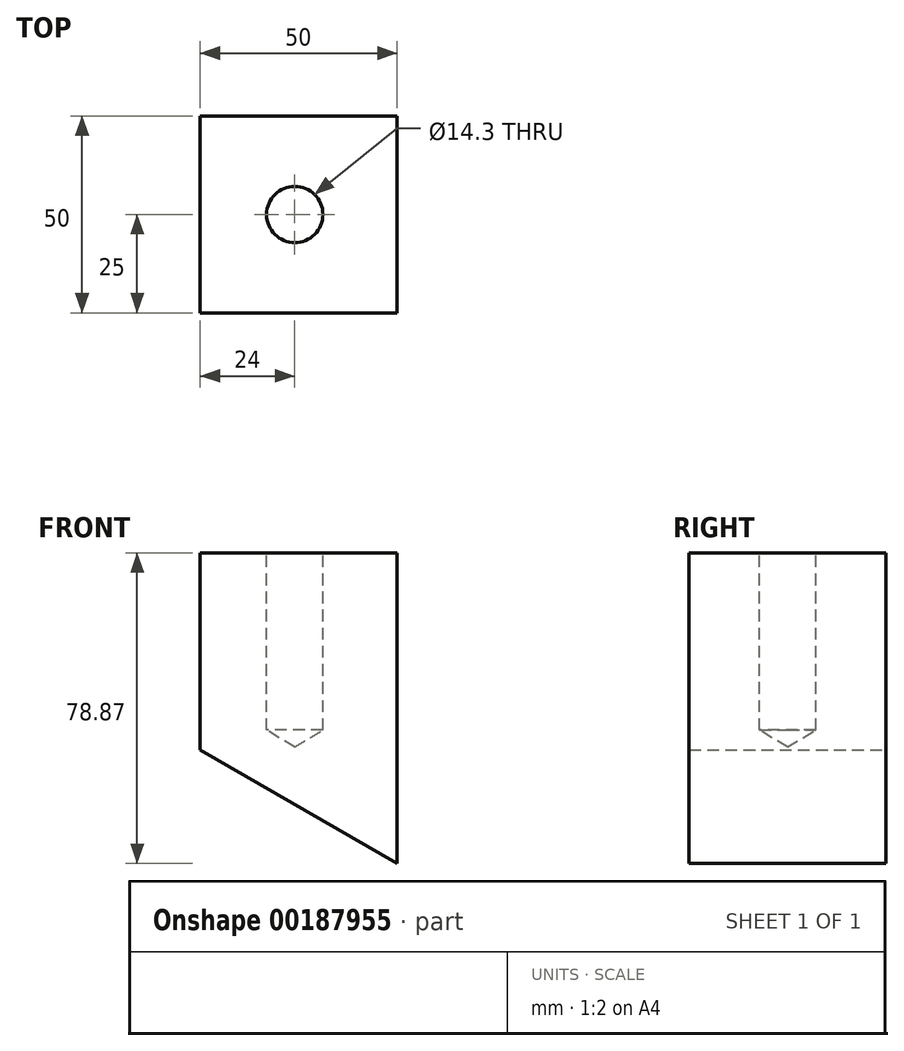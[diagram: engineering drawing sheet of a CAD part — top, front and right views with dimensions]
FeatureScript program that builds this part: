
annotation { "Feature Type Name" : "Feature", "Feature Type Description" : "" }
export const myFeature = defineFeature(function(context is Context, id is Id, definition is map)
    precondition{}
    {
        {
            var Q0;
            Q0=qCreatedBy(makeId("Front.planeOp"),FACE);
            var sketch = newSketch(context, id + "F0", { "sketchPlane" : qUnion([Q0])});
            skLineSegment(sketch, "E0", {"start": v(0, 0) * mm, "end": v(-24, 0) * mm});
            skLineSegment(sketch, "E1", {"start": v(-24, 0) * mm, "end": v(-24, -50) * mm});
            skLineSegment(sketch, "E2", {"start": v(-24, -50) * mm, "end": v(26, -78.87) * mm});
            skLineSegment(sketch, "E3", {"start": v(26, -78.87) * mm, "end": v(26, 0) * mm});
            skLineSegment(sketch, "E4", {"start": v(26, 0) * mm, "end": v(0, 0) * mm});
            skSolve(sketch);
        }
        {
            var Q0;
            Q0=makeQuery(id+"F0.imprint","IMPRINT",FACE,{"disambiguationData":[TD([[makeQuery(id+"F0.imprint","IMPRINT",EDGE,{"derivedFrom":sQuery(id+"F0.wireOp",EDGE,"E0")}),1.0]])]});
            extrude(context, id + "F1", {"entities" : qUnion([Q0]), "endBound" : BoundingType.SYMMETRIC, "depth" : 50 * mm});
        }
        {
            var Q0;
            Q0=makeQuery(id+"F1.opExtrude","SWEPT_FACE",FACE,{"disambiguationData":[OSD([sQuery(id+"F0.wireOp",EDGE,"E0"),sQuery(id+"F0.wireOp",EDGE,"E4")])]});
            var sketch = newSketch(context, id + "F2", { "sketchPlane" : qUnion([Q0])});
            skPoint(sketch, "E5", {"position": v(0, 0) * mm});
            skSolve(sketch);
        }
        {
            var Q0;
            Q0=sQuery(id+"F2.wireOp",VERTEX,"E5");
            var Q1;
            Q1=makeQuery(id+"F1.opExtrude","SWEPT_BODY",BODY,{"disambiguationData":[OSD([sQuery(id+"F0.wireOp",EDGE,"E0"),sQuery(id+"F0.wireOp",EDGE,"E1"),sQuery(id+"F0.wireOp",EDGE,"E2"),sQuery(id+"F0.wireOp",EDGE,"E3"),sQuery(id+"F0.wireOp",EDGE,"E4")])]});
            hole(context, id + "F3", {"style" : HoleStyle.SIMPLE, "endStyle" : HoleEndStyle.BLIND, "holeDiameter" : 14.3 * mm, "holeDepth" : 45 * mm, "startFromSketch" : true, "locations" : qUnion([Q0]), "scope" : qUnion([Q1])});
        }
    });
